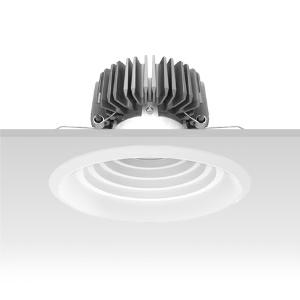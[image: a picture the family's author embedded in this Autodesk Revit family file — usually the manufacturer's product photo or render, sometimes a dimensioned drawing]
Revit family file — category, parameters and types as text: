
# Revit family: 3f_filippi_-_3f_reno_bianco_ugr_3f_filippi_-_30762_-_3f_reno_200_wh_2500-930_dali_ugr
name_source: partatom
category: Lighting Fixtures
units: mm (PartAtom-declared; Revit-internal decimal feet)

## family parameters
Cut with Voids When Loaded = No
Host = Face
Light Source = No
Part Type = Normal
Room Calculation Point = No
Round Connector Dimension = Use Diameter
Shared = No

## types (1)
- 3F Filippi - 3F Reno Bianco UGR (1 x LED, 2689 lm, 29 W, 3000 K)
    Apparent Load = 29 VA
    Approval mark = CE
    CIE Flux Codes = 90 100 100 100 100
    Color Rendering = 90
    Color Temperature = 3000 K
    Control Gear = Electronic transformer
    Default Elevation = 1800 mm
    Description = ILLUMINOTECHNICAL
Luminous efficiency 100% (DLOR 100%, ULOR 0%).
Initial luminous flux of the luminaire 2689 lm.
Direct symmetric UGR distribution.
Installation Interdistance Transv.D = 0.99 x hu - Long.D = 1.01 x hu.
Average luminance <500 cd/m² for radial angles >65°.
Tabular UGR (CIE 117 - 4H-8H; S=0.25H; 70/50/20): RUG 17.7 - 17.6.
Beam angle: 64° - 65°.
Luminous efficacy 93 lm/W.
Lifetime (L90/B10): 30000 h. (tq+25°C)
Lifetime (L85/B10): 50000 h. (tq+25°C)
Lifetime (L70/B10): 80000 h. (tq+25°C)
Sudden decreased luminous flux after 50000 hours: 0% (C0).
Photobiological safety in compliance with IEC/TR 62778: RG1 low risk, (IEC 62471).
In compliance with IEC/EN 62722-2-1 - IEC/EN 62717 standards.

SOURCE
Compact LED module 2500/930.
Energy efficiency class (UE 2019/2020 - UE 2019/2015): F.
CIE 13.3 Colour rendering index: CRI >90 (R9 >50%).
IES TM-30 Fidelity Index: Rf = 92 Rg = 101.
CCT nominal colour temperature 3000 K.
Colour initial tolerance (MacAdam): SDCM 3.
Zhaga Book 3 compliant.

MECHANICAL
Passive heat dissipator in die-casting aluminium, oversized, for optimum thermal management of the LED module.
Parabolic element with graduated/concentric rings in white polycarbonate.
Internal specular metallic louvre to optimise control of the luminous flux in polycarbonate.
Transparent external lens with glossy and satin differentiated surfaces, with a cooling and anti-insect system in methacrylate (PMMA).
Fastening spring clips in stainless steel.
Dimensions: diameter 216 mm, height 142 mm. Weight 1.55 kg.
IP44 protection degree for exposed part, IP20 for recessed part.
Mechanical strength to impacts IK04 (0.5 joule).
Glow-wire test resistance 650°C.

ELECTRICAL
Wiring on a separate unit.
Halogen Free DALI-2 DATI (Parts 251, 252, 253), PUSH-DIM, electronic wiring 230V-50/60Hz, power factor 0.95 at full load, THD <25%, constant output current, SELV, class II, 1 driver, 1 DALI addresse.
Power of the luminaire 29 W.
ENEC - CE.
SAFE FLICKER: PstLM=<1 and SVM=<0.4 (IEC TR 61547-1 and IEC TR 63158), to ensure a more comfortable and safe light.
Luminaire compliant with EN 60598-2-22 for power supply from a centralised emergency system CPSS (Central Power Supply System), not incorporated in the luminaire - high risk areas excluded. The default power and flux are 100% in AC and 100% in DC.
Ambient temperature from 0°C to +25°C.
Temperature class T6 max 85°C.
Relative humidity UR: <85%.

INSTALLATION
Pull-up recessed fitting.
False ceiling carving: 200 mm.
All accessories dedicated to this product are available on the Catalog and on our website www.3F-Filippi.com.

APPLICATIONS
In environments with VDTs, managerial offices and staterooms, public offices and schools.
In false ceilings with narrow voids.

LIGHT MANAGEMENT
Recommended minimum setting: 10%.
The luminaire, equipped with (DALI-2 DATI) driver, can be controlled manually with 3F Easy Dim technology or automatically/manually with wired or wireless DALI/D2D control systems.
The D2D driver guarantees interoperability with other devices with the same certification by making the following information available:
Device Data (Part 251), Energy Report (Part 252), Diagnosis & Maintenance (Part 253).
In electrical systems without a regulation system (manual or automatic) and DALI bus, a suitable jumper must be made on the DA-DA terminals of the appliance.

WARNING
Luminaire designed for disposal/recycling at end-of-life.
Replaceable (LED only) light source by a professional. Replaceable control gear by a professional.
    Height = 0 mm  [stored 0 ft]
    Lamp = 1 x LED
    Lamp Light Flux = 2689 lm
    Lamp Power = 29 W
    Lamp count = 1
    Length = 216 mm
    Lifetime = 50000 h
    Luminous efficacy = 93 lm/W
    Manufacturer = 3F Filippi
    ModVariant = No
    Model = 3F Filippi - 30762 - 3F Reno 200 WH 2500-930 DALI UGR
    Mounting Place = Ceiling
    Mounting Type = Recessed
    Number of Poles = 1
    OnlyDefault = Yes
    Power Factor = 1
    Product Name = 3F Filippi - 3F Reno Bianco UGR
    Product group = recessed luminaire
    ProductGroupID = 4
    Protection Class = Protection class II
    Protection Degree = IP 20
    RLX_Detail_Level = 1
    RLX_Emergency_Light_Flux = 0 lm
    RLX_Emergency_Type = 0
    RLX_Emergency_Type_DB = No
    RlxData = <blob elided: 95321 chars, md5=5d0050d0>
    Socket = socket
    Standby Power = 0 W
    System Light Flux = 2689 lm
    System Power = 29 W
    Type Comments = Product without accessories
    Type Image = 3ffilippi_3f_reno_200_wh_2500_3000_4000.jpg
    URL = http://relux.com
    VarID = ---
    Voltage = 0 V
    Weight = 0.00 kg
    Width = 0 mm  [stored 0 ft]

note: [stored X ft] marks values corroborated as IEEE doubles in the binary element streams (Revit-internal decimal feet)

## geometry (parser evidence)
native form markers: Blend x4, Sweep x10
no freeform markers — native parametric forms only
